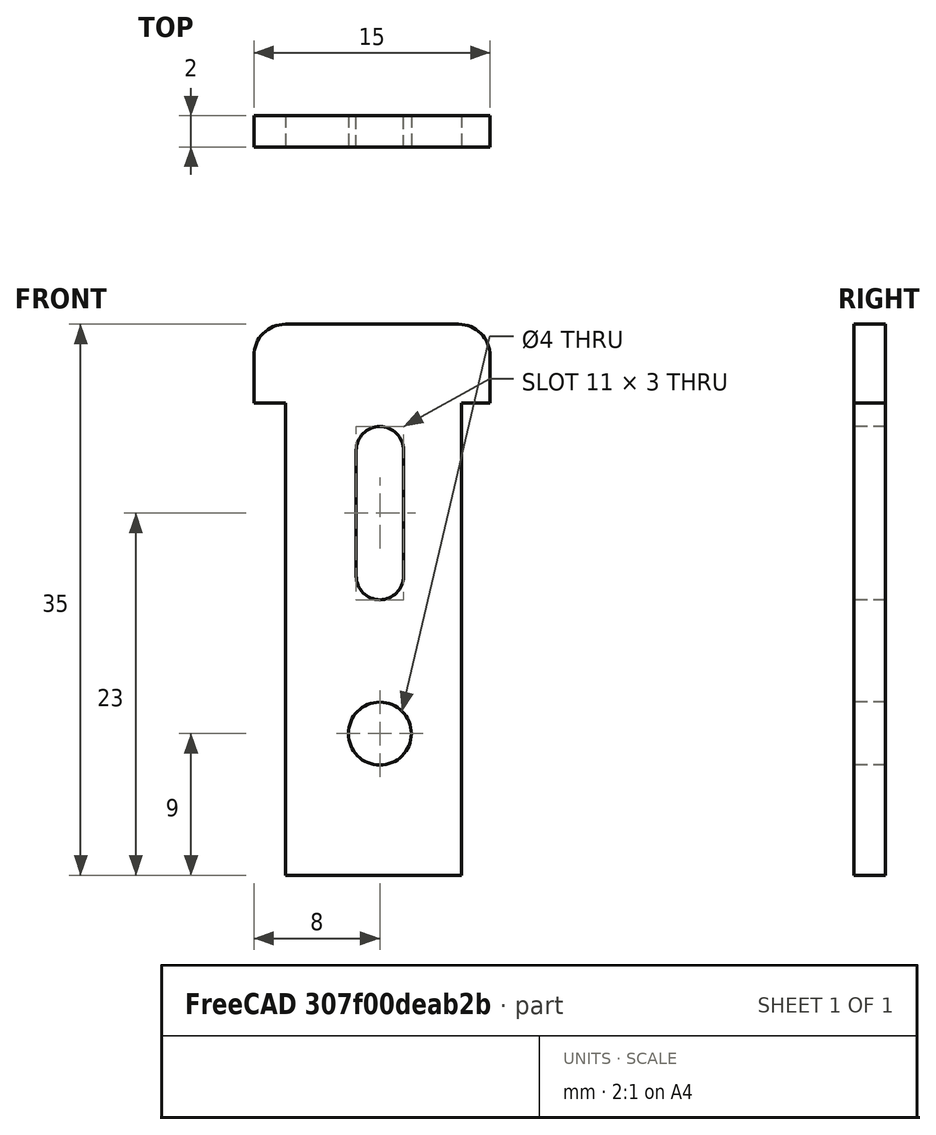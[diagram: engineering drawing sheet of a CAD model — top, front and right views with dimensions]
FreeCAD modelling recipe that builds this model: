
FCSTD DOCUMENT  (FreeCAD 0.17R13541 (Git))
Label: separador
License: All rights reserved
LicenseURL: http://en.wikipedia.org/wiki/All_rights_reserved
objects: Part::Box×3, Part::Cylinder×3, Part::MultiFuse×2, Part::Cut×1, Part::Fillet×1, Part::Feature×1, Mesh::Feature×1
note: 11 computed .brp shape members not serialized (recipe doc carries the construction recipe); baked Part::Feature solids carry a one-line shape summary decoded from their .brp

FEATURE [Part::Box] Box009  label="Cubo008"
  AttacherType = Attacher::AttachEngine3D
  Height = 8
  Length = 3
  Placement = pos=(86,32,-8) rot=(0,0,1;0rad)
  Width = 10
FEATURE [Part::Cylinder] Cylinder021  label="Cilindro021"
  Angle = 360
  AttacherType = Attacher::AttachEngine3D
  Height = 10
  Placement = pos=(87.5,41.5,0) rot=(1,0,0;1.5708rad)
  Radius = 1.5
FEATURE [Part::Box] Box007  label="Cubo006"
  AttacherType = Attacher::AttachEngine3D
  Height = 33
  Length = 11.2
  Placement = pos=(81.5,35.5,-27) rot=(0,0,1;0rad)
  Width = 2
FEATURE [Part::Cylinder] Cylinder022  label="Cilindro022"
  Angle = 360
  AttacherType = Attacher::AttachEngine3D
  Height = 10
  Placement = pos=(87.5,41.5,-8) rot=(1,0,0;1.5708rad)
  Radius = 1.5
FEATURE [Part::Cylinder] Cylinder023  label="Cilindro023"
  Angle = 360
  AttacherType = Attacher::AttachEngine3D
  Height = 10
  Placement = pos=(87.5,41.5,-18) rot=(1,0,0;1.5708rad)
  Radius = 2
FEATURE [Part::MultiFuse] Fusion006
  Shapes = -> [Box009,Cylinder022,Cylinder021,Cylinder023]
FEATURE [Part::Box] Box008  label="Cubo007"
  AttacherType = Attacher::AttachEngine3D
  Height = 5
  Length = 15
  Placement = pos=(79.5,35.5,3) rot=(0,0,1;0rad)
  Width = 2
FEATURE [Part::MultiFuse] Fusion005
  Shapes = -> [Box007,Box008]
FEATURE [Part::Cut] Cut
  Base = -> Fusion005
  Tool = -> Fusion006
FEATURE [Part::Fillet] Fillet  label="separador"
  Base = -> Cut
  Edges = 2 edges r=2: [Edge46,Edge47]
FEATURE [Part::Feature] Fillet_solid  label="separador (Solid)"
  shape: bbox 15 x 2 x 35 mm, 21 faces (baked)
FEATURE [Mesh::Feature] Mesh  label="separador (Solid) (Meshed)"
